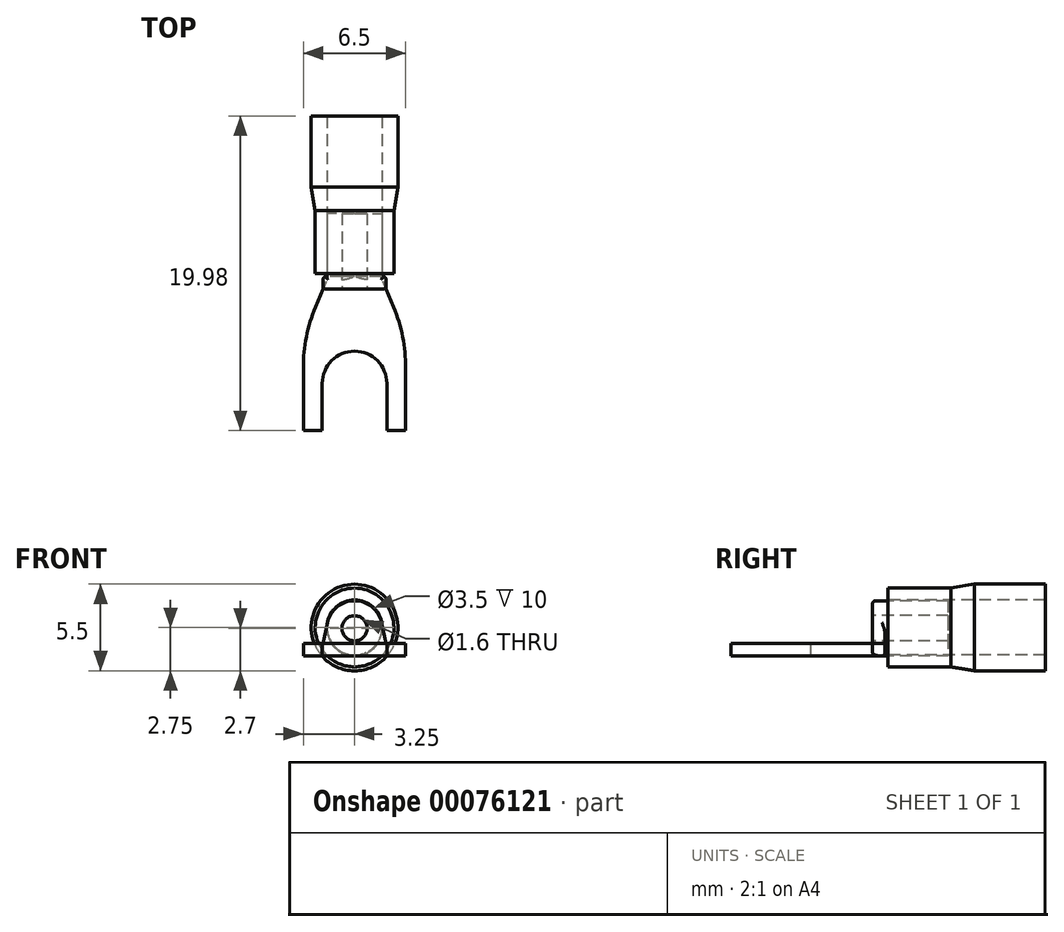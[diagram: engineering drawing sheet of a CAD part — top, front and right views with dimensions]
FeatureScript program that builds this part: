
annotation { "Feature Type Name" : "Feature", "Feature Type Description" : "" }
export const myFeature = defineFeature(function(context is Context, id is Id, definition is map)
    precondition{}
    {
        {
            var Q0;
            Q0=qCreatedBy(makeId("Top.planeOp"),FACE);
            var sketch = newSketch(context, id + "F0", { "sketchPlane" : qUnion([Q0])});
            skLineSegment(sketch, "E0.bottom", {"start": v(2, 4.52) * mm, "end": v(-2, 4.52) * mm});
            skLineSegment(sketch, "E0.top", {"start": v(3.25, -4.48) * mm, "end": v(2.05, -4.48) * mm});
            skLineSegment(sketch, "E0.left", {"start": v(3.25, -0.48) * mm, "end": v(3.25, -4.48) * mm});
            skLineSegment(sketch, "E0.right", {"start": v(-3.25, -0.48) * mm, "end": v(-3.25, -4.48) * mm});
            skPoint(sketch, "E0.middle", {"position": v(0, 0) * mm});
            skLineSegment(sketch, "E1", {"start": v(2.05, -4.48) * mm, "end": v(2.05, -1.48) * mm});
            skLineSegment(sketch, "E2", {"start": v(-2.05, -4.48) * mm, "end": v(-2.05, -1.48) * mm});
            skArc(sketch, "E3", {"start": v(-2.05, -1.48) * mm, "mid": v(0, 0.57) * mm, "end": v(2.05, -1.48) * mm});
            skLineSegment(sketch, "E4", {"start": v(-2.48, 3.37) * mm, "end": v(-2, 4.52) * mm});
            skLineSegment(sketch, "E5", {"start": v(2.48, 3.37) * mm, "end": v(2, 4.52) * mm});
            skLineSegment(sketch, "E6", {"start": v(0, -4.48) * mm, "end": v(0, 4.52) * mm, "construction": true});
            skPoint(sketch, "E6.endSnap0", {"position": v(0, 0.57) * mm});
            skLineSegment(sketch, "E7.trimOffspring", {"start": v(-2.05, -4.48) * mm, "end": v(-3.25, -4.48) * mm});
            skPoint(sketch, "E8.visualSharp", {"position": v(-3.25, 1.52) * mm});
            skArc(sketch, "E8.filletArc", {"start": v(-2.48, 3.37) * mm, "mid": v(-3.06, 1.48) * mm, "end": v(-3.25, -0.48) * mm});
            skPoint(sketch, "E9.visualSharp", {"position": v(3.25, 1.52) * mm});
            skArc(sketch, "E9.filletArc", {"start": v(3.25, -0.48) * mm, "mid": v(3.06, 1.48) * mm, "end": v(2.48, 3.37) * mm});
            skSolve(sketch);
        }
        {
            var Q0;
            Q0 = qSketchRegion(id + "F0", true);
            extrude(context, id + "F1", {"entities" : qUnion([Q0]), "depth" : 0.8 * mm});
        }
        {
            var Q0;
            Q0=makeQuery(id+"F1.opExtrude","SWEPT_FACE",FACE,{"disambiguationData":[OSD([sQuery(id+"F0.wireOp",EDGE,"E0.bottom")])]});
            var sketch = newSketch(context, id + "F2", { "sketchPlane" : qUnion([Q0])});
            skCircle(sketch, "E10", {"center": v(0, 1.75) * mm, "radius": 0.8 * mm});
            skArc(sketch, "E11", {"start": v(1.7, 2.12) * mm, "mid": v(0, 3.5) * mm, "end": v(-1.7, 2.12) * mm});
            skLineSegment(sketch, "E12", {"start": v(-2, 0) * mm, "end": v(-2, 0.8) * mm});
            skLineSegment(sketch, "E13", {"start": v(-2, 0.8) * mm, "end": v(-1.7, 2.12) * mm});
            skLineSegment(sketch, "E14", {"start": v(2, 0) * mm, "end": v(2, 0.8) * mm});
            skLineSegment(sketch, "E15", {"start": v(2, 0.8) * mm, "end": v(1.7, 2.12) * mm});
            skLineSegment(sketch, "E16", {"start": v(-2, 0) * mm, "end": v(2, 0) * mm});
            skSolve(sketch);
        }
        {
            var Q0;
            Q0 = qSketchRegion(id + "F2", true);
            extrude(context, id + "F3", {"entities" : qUnion([Q0]), "operationType" : NewBodyOperationType.ADD, "depth" : 0.8 * mm});
        }
        {
            var Q0;
            Q0=makeQuery(id+"F3.opExtrude","CAP_FACE",FACE,{"disambiguationData":[OSD([sQuery(id+"F2.wireOp",EDGE,"E10"),sQuery(id+"F2.wireOp",EDGE,"E11"),sQuery(id+"F2.wireOp",EDGE,"E12"),sQuery(id+"F2.wireOp",EDGE,"E13"),sQuery(id+"F2.wireOp",EDGE,"E14"),sQuery(id+"F2.wireOp",EDGE,"E15"),sQuery(id+"F2.wireOp",EDGE,"E16")])],"isStart":false});
            var sketch = newSketch(context, id + "F4", { "sketchPlane" : qUnion([Q0])});
            skCircle(sketch, "E17", {"center": v(0, 1.75) * mm, "radius": 1.75 * mm});
            skCircle(sketch, "E18", {"center": v(0, 1.75) * mm, "radius": 0.8 * mm});
            skSolve(sketch);
        }
        {
            var Q0;
            Q0 = qSketchRegion(id + "F4", true);
            extrude(context, id + "F5", {"entities" : qUnion([Q0]), "operationType" : NewBodyOperationType.ADD, "depth" : 4 * mm});
        }
        {
            var Q0;
            {var subQ0=sQuery(id+"F2.wireOp",EDGE,"E13");var subQ3=sQuery(id+"F4.wireOp",EDGE,"E17");Q0=makeQuery(id+"F5.boolean.opBoolean","SPLIT",EDGE,{"disambiguationData":[TD([makeQuery(id+"F3.opExtrude","SWEPT_FACE",FACE,{"disambiguationData":[OSD([subQ0])]})])],"derivedFrom":makeQuery(id+"F5.opExtrude","CAP_EDGE",EDGE,{"disambiguationData":[OSD([subQ3])],"isStart":true})});}
            var Q1;
            {var subQ0=sQuery(id+"F2.wireOp",EDGE,"E15");var subQ3=sQuery(id+"F4.wireOp",EDGE,"E17");Q1=makeQuery(id+"F5.boolean.opBoolean","SPLIT",EDGE,{"disambiguationData":[TD([makeQuery(id+"F3.opExtrude","SWEPT_FACE",FACE,{"disambiguationData":[OSD([subQ0])]})])],"derivedFrom":makeQuery(id+"F5.opExtrude","CAP_EDGE",EDGE,{"disambiguationData":[OSD([subQ3])],"isStart":true})});}
            var Q2;
            Q2=makeQuery(id+"F3.opExtrude","CAP_EDGE",EDGE,{"disambiguationData":[OSD([sQuery(id+"F2.wireOp",EDGE,"E14")])],"isStart":false});
            var Q3;
            {var subQ0=sQuery(id+"F2.wireOp",EDGE,"E14");var subQ2=sQuery(id+"F2.wireOp",EDGE,"E16");Q3=makeQuery(id+"F5.boolean.opBoolean","SPLIT",EDGE,{"disambiguationData":[TD([makeQuery(id+"F3.opExtrude","SWEPT_FACE",FACE,{"disambiguationData":[OSD([subQ0])]})])],"derivedFrom":makeQuery(id+"F3.opExtrude","CAP_EDGE",EDGE,{"disambiguationData":[OSD([subQ2])],"isStart":false})});}
            var Q4;
            {var subQ0=sQuery(id+"F2.wireOp",EDGE,"E12");var subQ2=sQuery(id+"F2.wireOp",EDGE,"E16");Q4=makeQuery(id+"F5.boolean.opBoolean","SPLIT",EDGE,{"disambiguationData":[TD([makeQuery(id+"F3.opExtrude","SWEPT_FACE",FACE,{"disambiguationData":[OSD([subQ0])]})])],"derivedFrom":makeQuery(id+"F3.opExtrude","CAP_EDGE",EDGE,{"disambiguationData":[OSD([subQ2])],"isStart":false})});}
            var Q5;
            Q5=makeQuery(id+"F3.opExtrude","CAP_EDGE",EDGE,{"disambiguationData":[OSD([sQuery(id+"F2.wireOp",EDGE,"E12")])],"isStart":false});
            var Q6;
            Q6=makeQuery(id+"F3.opExtrude","CAP_EDGE",EDGE,{"disambiguationData":[OSD([sQuery(id+"F2.wireOp",EDGE,"E13")])],"isStart":false});
            var Q7;
            Q7=makeQuery(id+"F3.opExtrude","CAP_EDGE",EDGE,{"disambiguationData":[OSD([sQuery(id+"F2.wireOp",EDGE,"E15")])],"isStart":false});
            var Q8;
            Q8=makeQuery(id+"F3.opExtrude","SWEPT_EDGE",EDGE,{"disambiguationData":[OSD([sQuery(id+"F2.wireOp",EDGE,"E14"),sQuery(id+"F2.wireOp",EDGE,"E16")])]});
            var Q9;
            Q9=makeQuery(id+"F3.opExtrude","SWEPT_EDGE",EDGE,{"disambiguationData":[OSD([sQuery(id+"F2.wireOp",EDGE,"E12"),sQuery(id+"F2.wireOp",EDGE,"E16")])]});
            var Q10;
            Q10=makeQuery(id+"F3.opExtrude","CAP_EDGE",EDGE,{"disambiguationData":[OSD([sQuery(id+"F2.wireOp",EDGE,"E13")])],"isStart":true});
            var Q11;
            Q11=makeQuery(id+"F3.opExtrude","CAP_EDGE",EDGE,{"disambiguationData":[OSD([sQuery(id+"F2.wireOp",EDGE,"E11")])],"isStart":true});
            fillet(context, id + "F6", {"entities" : qUnion([Q0, Q1, Q2, Q3, Q4, Q5, Q6, Q7, Q8, Q9, Q10, Q11]), "radius" : 0.2 * mm, "tangentPropagation" : true, "allowEdgeOverflow" : false});
        }
        {
            var Q0;
            Q0=makeQuery(id+"F1.opExtrude","CAP_FACE",FACE,{"disambiguationData":[OSD([sQuery(id+"F0.wireOp",EDGE,"E0.bottom"),sQuery(id+"F0.wireOp",EDGE,"E0.top"),sQuery(id+"F0.wireOp",EDGE,"E0.left"),sQuery(id+"F0.wireOp",EDGE,"E0.right"),sQuery(id+"F0.wireOp",EDGE,"E1"),sQuery(id+"F0.wireOp",EDGE,"E2"),sQuery(id+"F0.wireOp",EDGE,"E3"),sQuery(id+"F0.wireOp",EDGE,"E4"),sQuery(id+"F0.wireOp",EDGE,"E5"),sQuery(id+"F0.wireOp",EDGE,"E7.trimOffspring"),sQuery(id+"F0.wireOp",EDGE,"E8.filletArc"),sQuery(id+"F0.wireOp",EDGE,"E9.filletArc")])],"isStart":false});
            cPlane(context, id + "F7", {"entities" : qUnion([Q0]), "cplaneType" : CPlaneType.OFFSET, "offset" : 1 * mm, "width" : 150 * mm, "height" : 150 * mm});
        }
        {
            var Q0;
            Q0=qCreatedBy(id+"F7.planeOp",FACE);
            var sketch = newSketch(context, id + "F8", { "sketchPlane" : qUnion([Q0])});
            skLineSegment(sketch, "E19", {"start": v(0, 5.5) * mm, "end": v(0, 15.5) * mm, "construction": true});
            skLineSegment(sketch, "E20", {"start": v(-1.75, 5.5) * mm, "end": v(-1.75, 15.5) * mm});
            skLineSegment(sketch, "E21", {"start": v(-1.75, 15.5) * mm, "end": v(-2.75, 15.5) * mm});
            skLineSegment(sketch, "E22", {"start": v(-2.75, 15.5) * mm, "end": v(-2.75, 11) * mm});
            skLineSegment(sketch, "E23", {"start": v(-2.5, 9.5) * mm, "end": v(-2.5, 5.5) * mm});
            skLineSegment(sketch, "E24", {"start": v(-2.5, 5.5) * mm, "end": v(-1.75, 5.5) * mm});
            skLineSegment(sketch, "E25", {"start": v(-2.75, 11) * mm, "end": v(-2.5, 9.5) * mm});
            skSolve(sketch);
        }
        {
            var Q0;
            Q0 = qSketchRegion(id + "F8", true);
            var Q1;
            Q1=sQuery(id+"F8.wireOp",EDGE,"E19");
            revolve(context, id + "F9", {"entities" : qUnion([Q0]), "axis" : qUnion([Q1]), "revolveType" : RevolveType.FULL});
        }
    });
